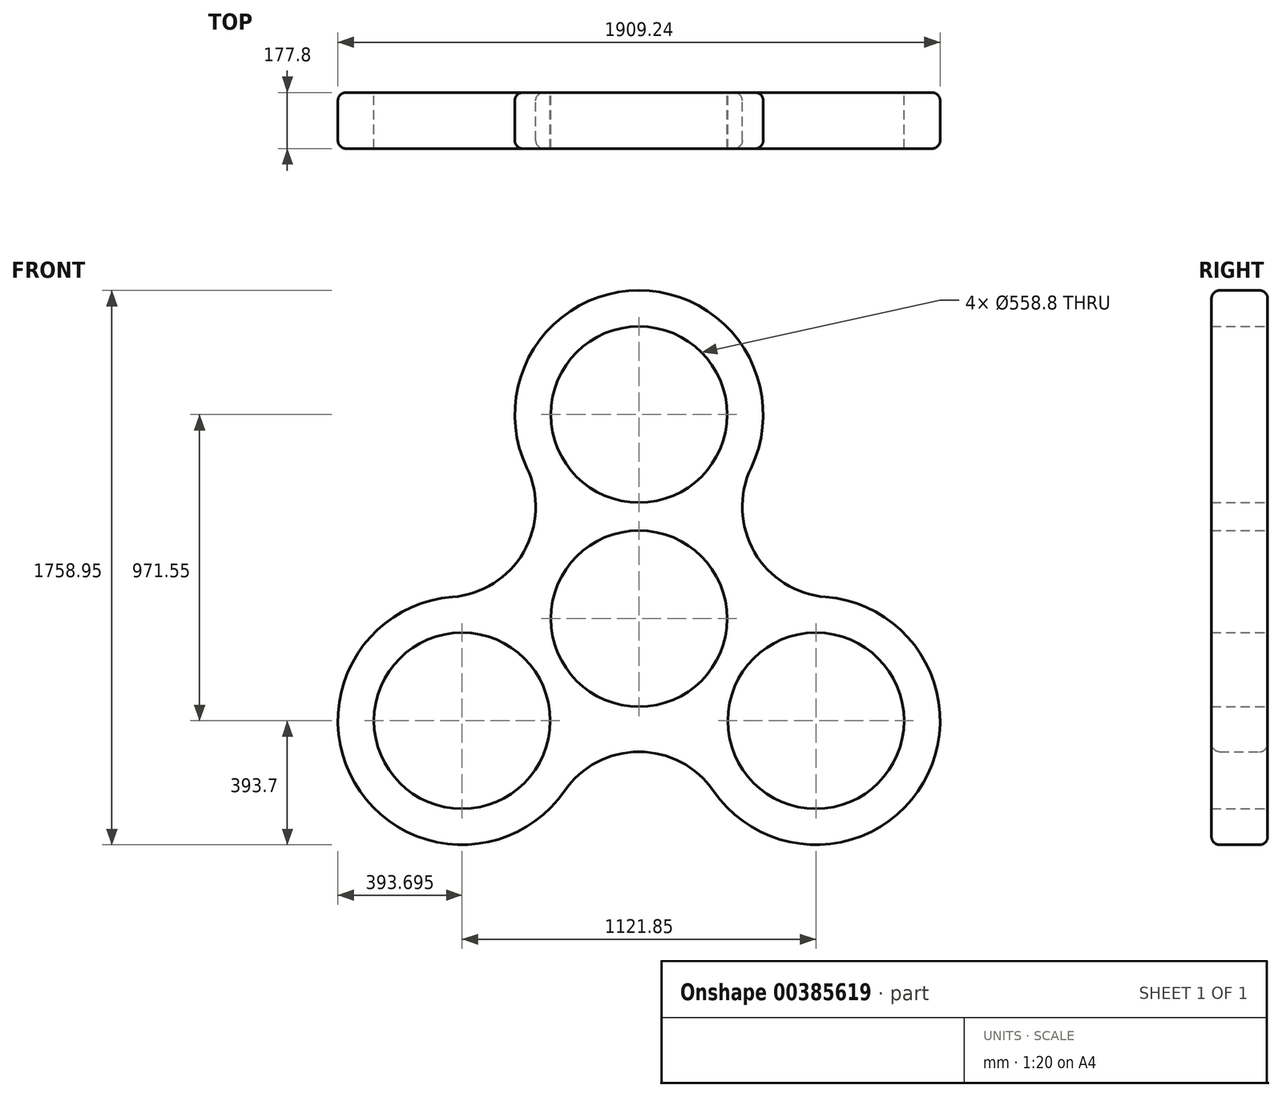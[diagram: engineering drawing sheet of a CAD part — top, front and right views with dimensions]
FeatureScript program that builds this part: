
annotation { "Feature Type Name" : "Feature", "Feature Type Description" : "" }
export const myFeature = defineFeature(function(context is Context, id is Id, definition is map)
    precondition{}
    {
        {
            var Q0;
            Q0=qCreatedBy(makeId("Front.planeOp"),FACE);
            var sketch = newSketch(context, id + "F0", { "sketchPlane" : qUnion([Q0])});
            skCircle(sketch, "E0", {"center": v(0, 647.7) * mm, "radius": 279.4 * mm});
            skCircle(sketch, "E1", {"center": v(0, 0) * mm, "radius": 279.4 * mm});
            skPoint(sketch, "E2.center", {"position": v(0, -0.04) * mm});
            skLineSegment(sketch, "E3.anchor1", {"start": v(0, -0.04) * mm, "end": v(0, -0.04) * mm});
            skLineSegment(sketch, "E3.anchor2", {"start": v(0, -0.04) * mm, "end": v(0, -0.04) * mm});
            skArc(sketch, "E4.converted", {"start": v(355.38, 478.28) * mm, "mid": v(0, 1041.4) * mm, "end": v(-355.38, 478.28) * mm});
            skArc(sketch, "E5.1.0", {"start": v(-591.89, 68.63) * mm, "mid": v(-901.88, -520.7) * mm, "end": v(-236.5, -546.9) * mm});
            skCircle(sketch, "E5.1.1", {"center": v(-560.92, -323.85) * mm, "radius": 279.4 * mm});
            skArc(sketch, "E5.2.0", {"start": v(236.5, -546.9) * mm, "mid": v(901.88, -520.7) * mm, "end": v(591.89, 68.63) * mm});
            skCircle(sketch, "E5.2.1", {"center": v(560.92, -323.85) * mm, "radius": 279.4 * mm});
            skArc(sketch, "E6", {"start": v(355.38, 478.28) * mm, "mid": v(365.9, 211.25) * mm, "end": v(591.89, 68.63) * mm});
            skArc(sketch, "E7", {"start": v(-591.89, 68.63) * mm, "mid": v(-365.9, 211.25) * mm, "end": v(-355.38, 478.28) * mm});
            skArc(sketch, "E8", {"start": v(236.5, -546.9) * mm, "mid": v(0, -422.5) * mm, "end": v(-236.5, -546.9) * mm});
            skSolve(sketch);
        }
        {
            var Q0;
            Q0=makeQuery(id+"F0.imprint","IMPRINT",FACE,{"disambiguationData":[TD([[makeQuery(id+"F0.imprint","IMPRINT",EDGE,{"derivedFrom":sQuery(id+"F0.wireOp",EDGE,"E0")}),-1.0]])]});
            extrude(context, id + "F1", {"entities" : qUnion([Q0]), "depth" : 177.8 * mm, "offsetDistance" : 25 * mm});
        }
        {
            var Q0;
            Q0=makeQuery(id+"F1.opExtrude","CAP_EDGE",EDGE,{"disambiguationData":[OSD([sQuery(id+"F0.wireOp",EDGE,"E4.converted")])],"isStart":false});
            var Q1;
            Q1=makeQuery(id+"F1.opExtrude","CAP_EDGE",EDGE,{"disambiguationData":[OSD([sQuery(id+"F0.wireOp",EDGE,"E4.converted")])],"isStart":true});
            fillet(context, id + "F2", {"entities" : qUnion([Q0, Q1]), "radius" : 25.4 * mm, "tangentPropagation" : true, "allowEdgeOverflow" : false});
        }
    });
